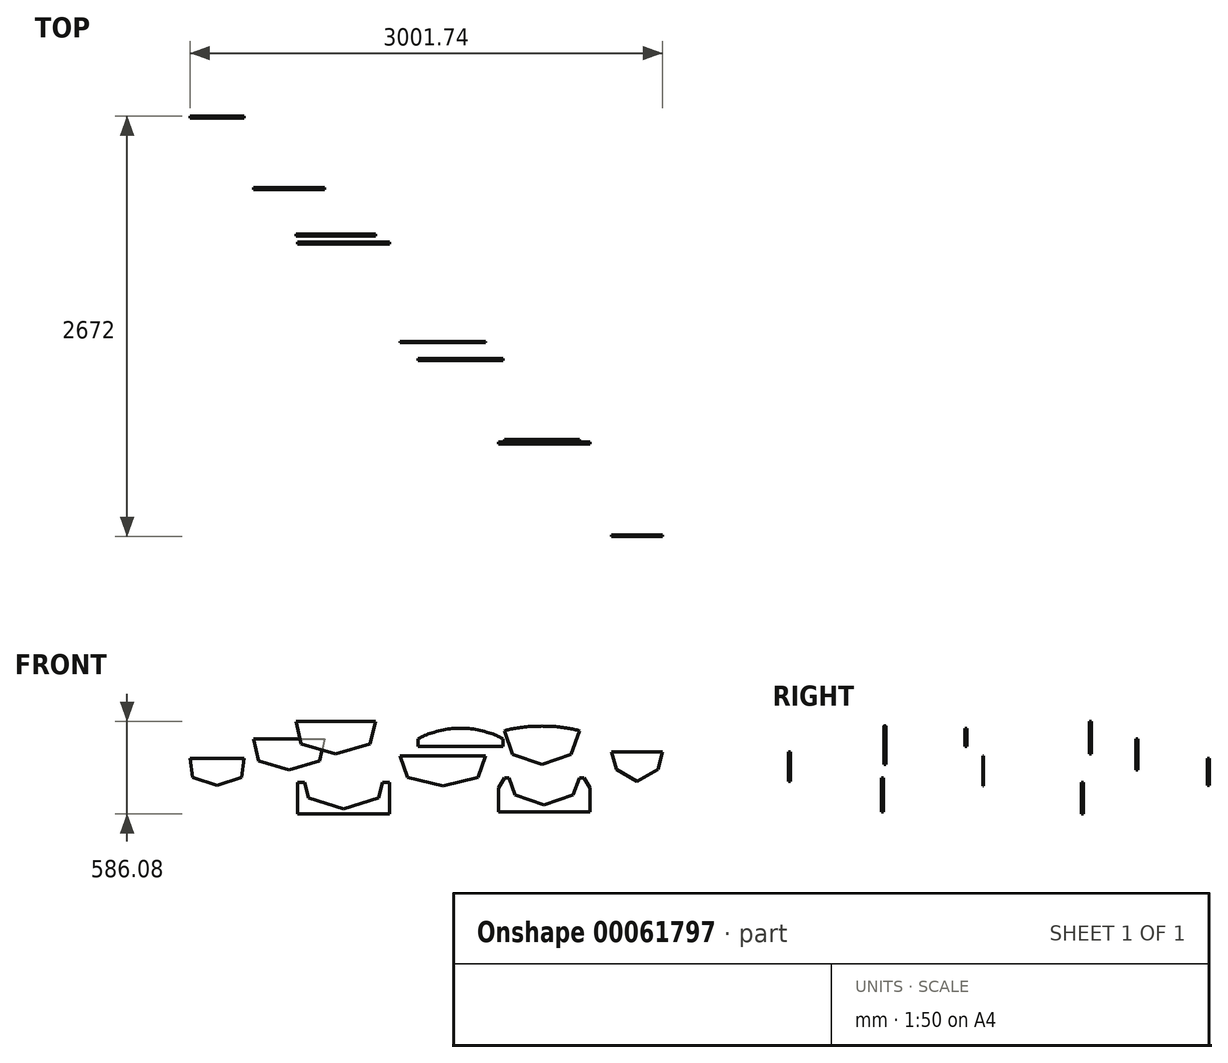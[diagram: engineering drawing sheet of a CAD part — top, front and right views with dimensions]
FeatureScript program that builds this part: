
annotation { "Feature Type Name" : "Feature", "Feature Type Description" : "" }
export const myFeature = defineFeature(function(context is Context, id is Id, definition is map)
    precondition{}
    {
        {
            var Q0;
            Q0=qCreatedBy(makeId("Front.planeOp"),FACE);
            var sketch = newSketch(context, id + "F0", { "sketchPlane" : qUnion([Q0])});
            skLineSegment(sketch, "E0", {"start": v(-1830.68, 262.65) * mm, "end": v(-1200, 262.65) * mm});
            skLineSegment(sketch, "E1", {"start": v(-1830.68, -139.62) * mm, "end": v(-1830.68, 4799.2) * mm, "construction": true});
            skLineSegment(sketch, "E2", {"start": v(-1881.52, 887.8) * mm, "end": v(-1881.52, 681.7) * mm, "construction": true});
            skLineSegment(sketch, "E3", {"start": v(-1881.52, 887.8) * mm, "end": v(-1629.48, 887.8) * mm});
            skLineSegment(sketch, "E4", {"start": v(-1629.48, 887.8) * mm, "end": v(-1663.3, 746.84) * mm});
            skLineSegment(sketch, "E5", {"start": v(-1663.3, 746.84) * mm, "end": v(-1881.52, 681.7) * mm});
            skLineSegment(sketch, "E6", {"start": v(-2176.59, 779.12) * mm, "end": v(-2176.59, 581.77) * mm, "construction": true});
            skLineSegment(sketch, "E7", {"start": v(-2176.59, 779.12) * mm, "end": v(-1951.82, 779.12) * mm});
            skLineSegment(sketch, "E8", {"start": v(-1951.82, 779.12) * mm, "end": v(-1983.36, 639.45) * mm});
            skLineSegment(sketch, "E9", {"start": v(-1983.36, 639.45) * mm, "end": v(-2176.59, 581.77) * mm});
            skLineSegment(sketch, "E10", {"start": v(-2634.04, 652.9) * mm, "end": v(-2634.04, 481.38) * mm, "construction": true});
            skLineSegment(sketch, "E11", {"start": v(-2634.04, 481.38) * mm, "end": v(-2477.4, 532.43) * mm});
            skLineSegment(sketch, "E12", {"start": v(-2477.4, 532.43) * mm, "end": v(-2462.07, 652.9) * mm});
            skLineSegment(sketch, "E13", {"start": v(-2462.07, 652.9) * mm, "end": v(-2634.04, 652.9) * mm});
            skLineSegment(sketch, "E14", {"start": v(-1830.68, 301.72) * mm, "end": v(-1830.68, 334.1) * mm, "construction": true});
            skLineSegment(sketch, "E15", {"start": v(-1830.68, 301.72) * mm, "end": v(-1538.96, 301.72) * mm});
            skLineSegment(sketch, "E16", {"start": v(-1538.96, 301.72) * mm, "end": v(-1538.96, 502.42) * mm});
            skLineSegment(sketch, "E17", {"start": v(-1538.96, 502.42) * mm, "end": v(-1583.2, 502.42) * mm});
            skLineSegment(sketch, "E18", {"start": v(-1583.2, 502.42) * mm, "end": v(-1609.22, 402.47) * mm});
            skLineSegment(sketch, "E19", {"start": v(-1609.22, 402.47) * mm, "end": v(-1830.68, 334.1) * mm});
            skLineSegment(sketch, "E20", {"start": v(-1200.8, 670.27) * mm, "end": v(-1200.8, 478.47) * mm, "construction": true});
            skLineSegment(sketch, "E21", {"start": v(-1200.8, 670.27) * mm, "end": v(-928.1, 670.27) * mm});
            skLineSegment(sketch, "E22", {"start": v(-928.1, 670.27) * mm, "end": v(-976.27, 533.92) * mm});
            skLineSegment(sketch, "E23", {"start": v(-976.27, 533.92) * mm, "end": v(-1200.8, 478.47) * mm});
            skLineSegment(sketch, "E24", {"start": v(-1088.15, 729.97) * mm, "end": v(-818.18, 729.97) * mm});
            skLineSegment(sketch, "E25", {"start": v(-818.18, 729.97) * mm, "end": v(-818.18, 778.33) * mm});
            skLineSegment(sketch, "E26", {"start": v(-1088.15, 729.97) * mm, "end": v(-1088.15, 845.89) * mm, "construction": true});
            skFitSpline(sketch, "E27", {"points": [v(-1088.15, 845.89) * mm, v(-1019.68, 840.48) * mm, v(-959.8, 829.65) * mm, v(-902.8, 814.5) * mm, v(-861.68, 799.35) * mm, v(-818.18, 778.33) * mm], "startDerivative": vector(314.76, -18.35) * mm, "endDerivative": vector(237.16, -119.9) * mm});
            skLineSegment(sketch, "E28", {"start": v(-571.9, 616.82) * mm, "end": v(-571.9, 859.2) * mm, "construction": true});
            skLineSegment(sketch, "E29", {"start": v(-571.9, 616.82) * mm, "end": v(-387.13, 679.24) * mm});
            skLineSegment(sketch, "E30", {"start": v(-387.13, 679.24) * mm, "end": v(-333.5, 829.26) * mm});
            skFitSpline(sketch, "E31", {"points": [v(-571.9, 859.2) * mm, v(-495.31, 856.38) * mm, v(-450.64, 851.56) * mm, v(-419.47, 847.38) * mm, v(-389.9, 842.56) * mm, v(-368.37, 838.39) * mm, v(-346.52, 833.57) * mm, v(-333.5, 829.26) * mm], "startDerivative": vector(367.92, -7.93) * mm, "endDerivative": vector(128.38, -47.16) * mm});
            skLineSegment(sketch, "E32", {"start": v(-557.3, 313.35) * mm, "end": v(-557.3, 357.58) * mm, "construction": true});
            skLineSegment(sketch, "E33", {"start": v(-557.3, 357.58) * mm, "end": v(-373.4, 422.9) * mm});
            skLineSegment(sketch, "E34", {"start": v(-373.4, 422.9) * mm, "end": v(-333.26, 530.39) * mm});
            skLineSegment(sketch, "E35", {"start": v(-333.26, 530.39) * mm, "end": v(-305.1, 530.39) * mm});
            skLineSegment(sketch, "E36", {"start": v(-305.1, 530.39) * mm, "end": v(-266.92, 466.71) * mm});
            skLineSegment(sketch, "E37", {"start": v(-266.92, 466.71) * mm, "end": v(-266.92, 313.35) * mm});
            skLineSegment(sketch, "E38", {"start": v(-557.3, 313.35) * mm, "end": v(-266.92, 313.35) * mm});
            skPoint(sketch, "E39.orphan", {"position": v(-266.92, 314.51) * mm});
            skLineSegment(sketch, "E40", {"start": v(33.12, 696.1) * mm, "end": v(33.12, 509.05) * mm, "construction": true});
            skLineSegment(sketch, "E41", {"start": v(33.12, 696.1) * mm, "end": v(195.74, 696.1) * mm});
            skLineSegment(sketch, "E42", {"start": v(195.74, 696.1) * mm, "end": v(164.42, 585.63) * mm});
            skLineSegment(sketch, "E43", {"start": v(164.42, 585.63) * mm, "end": v(33.12, 509.05) * mm});
            skSolve(sketch);
        }
        {
            var Q0;
            Q0=qCreatedBy(makeId("Front.planeOp"),FACE);
            cPlane(context, id + "F1", {"entities" : qUnion([Q0]), "cplaneType" : CPlaneType.OFFSET, "offset" : 50 * mm, "oppositeDirection" : true, "width" : 150 * mm, "height" : 150 * mm});
        }
        {
            var Q0;
            Q0=qCreatedBy(id+"F1.planeOp",FACE);
            var sketch = newSketch(context, id + "F2", { "sketchPlane" : qUnion([Q0])});
            skLineSegment(sketch, "E44.0", {"start": v(-1663.3, 746.84) * mm, "end": v(-1881.52, 681.7) * mm});
            skLineSegment(sketch, "E45.0", {"start": v(-1629.48, 887.8) * mm, "end": v(-1663.3, 746.84) * mm});
            skLineSegment(sketch, "E46.0", {"start": v(-1881.52, 887.8) * mm, "end": v(-1629.48, 887.8) * mm});
            skLineSegment(sketch, "E47.0", {"start": v(-1881.52, 887.8) * mm, "end": v(-1881.52, 681.7) * mm});
            skLineSegment(sketch, "E48.MirrorCS", {"start": v(-1881.52, 887.8) * mm, "end": v(-2133.56, 887.8) * mm});
            skLineSegment(sketch, "E49.MirrorCS", {"start": v(-2133.56, 887.8) * mm, "end": v(-2099.74, 746.84) * mm});
            skLineSegment(sketch, "E50.MirrorCS", {"start": v(-2099.74, 746.84) * mm, "end": v(-1881.52, 681.7) * mm});
            skSolve(sketch);
        }
        {
            var Q0;
            Q0 = qSketchRegion(id + "F2", true);
            extrude(context, id + "F3", {"entities" : qUnion([Q0]), "endBound" : BoundingType.SYMMETRIC, "depth" : 12 * mm});
        }
        {
            var Q0;
            Q0=qCreatedBy(makeId("Front.planeOp"),FACE);
            cPlane(context, id + "F4", {"entities" : qUnion([Q0]), "cplaneType" : CPlaneType.OFFSET, "offset" : 345 * mm, "oppositeDirection" : true, "width" : 150 * mm, "height" : 150 * mm});
        }
        {
            var Q0;
            Q0=qCreatedBy(id+"F4.planeOp",FACE);
            var sketch = newSketch(context, id + "F5", { "sketchPlane" : qUnion([Q0])});
            skLineSegment(sketch, "E51.0", {"start": v(-1983.36, 639.45) * mm, "end": v(-2176.59, 581.77) * mm});
            skLineSegment(sketch, "E51.1", {"start": v(-1951.82, 779.12) * mm, "end": v(-1983.36, 639.45) * mm});
            skLineSegment(sketch, "E51.2", {"start": v(-2176.59, 779.12) * mm, "end": v(-1951.82, 779.12) * mm});
            skLineSegment(sketch, "E51.3", {"start": v(-2176.59, 779.12) * mm, "end": v(-2176.59, 581.77) * mm});
            skLineSegment(sketch, "E52.MirrorCS", {"start": v(-2176.59, 779.12) * mm, "end": v(-2401.35, 779.12) * mm});
            skLineSegment(sketch, "E53.MirrorCS", {"start": v(-2401.35, 779.12) * mm, "end": v(-2369.8, 639.45) * mm});
            skLineSegment(sketch, "E54.MirrorCS", {"start": v(-2369.8, 639.45) * mm, "end": v(-2176.59, 581.77) * mm});
            skSolve(sketch);
        }
        {
            var Q0;
            Q0 = qSketchRegion(id + "F5", true);
            extrude(context, id + "F6", {"entities" : qUnion([Q0]), "endBound" : BoundingType.SYMMETRIC, "depth" : 12 * mm});
        }
        {
            var Q0;
            Q0=qCreatedBy(makeId("Front.planeOp"),FACE);
            var sketch = newSketch(context, id + "F7", { "sketchPlane" : qUnion([Q0])});
            skLineSegment(sketch, "E55.0", {"start": v(-1609.22, 402.47) * mm, "end": v(-1830.68, 334.1) * mm});
            skLineSegment(sketch, "E56.0", {"start": v(-1583.2, 502.42) * mm, "end": v(-1609.22, 402.47) * mm});
            skLineSegment(sketch, "E57.0", {"start": v(-1538.96, 502.42) * mm, "end": v(-1583.2, 502.42) * mm});
            skLineSegment(sketch, "E58.0", {"start": v(-1538.96, 301.72) * mm, "end": v(-1538.96, 502.42) * mm});
            skLineSegment(sketch, "E59.0", {"start": v(-1830.68, 301.72) * mm, "end": v(-1538.96, 301.72) * mm});
            skLineSegment(sketch, "E60.0", {"start": v(-1830.68, 301.72) * mm, "end": v(-1830.68, 334.1) * mm, "construction": true});
            skLineSegment(sketch, "E61", {"start": v(-1830.68, 334.1) * mm, "end": v(-1830.68, 301.72) * mm, "construction": true});
            skLineSegment(sketch, "E62.MirrorCS", {"start": v(-2052.14, 402.47) * mm, "end": v(-1830.68, 334.1) * mm});
            skLineSegment(sketch, "E63.MirrorCS", {"start": v(-2078.17, 502.42) * mm, "end": v(-2052.14, 402.47) * mm});
            skLineSegment(sketch, "E64.MirrorCS", {"start": v(-2122.4, 502.42) * mm, "end": v(-2078.17, 502.42) * mm});
            skLineSegment(sketch, "E65.MirrorCS", {"start": v(-2122.4, 301.72) * mm, "end": v(-2122.4, 502.42) * mm});
            skLineSegment(sketch, "E66.MirrorCS", {"start": v(-1830.68, 301.72) * mm, "end": v(-2122.4, 301.72) * mm});
            skSolve(sketch);
        }
        {
            var Q0;
            Q0 = qSketchRegion(id + "F7", true);
            extrude(context, id + "F8", {"entities" : qUnion([Q0]), "endBound" : BoundingType.SYMMETRIC, "depth" : 12 * mm});
        }
        {
            var Q0;
            Q0=qCreatedBy(makeId("Front.planeOp"),FACE);
            cPlane(context, id + "F9", {"entities" : qUnion([Q0]), "cplaneType" : CPlaneType.OFFSET, "offset" : 800 * mm, "oppositeDirection" : true, "width" : 150 * mm, "height" : 150 * mm});
        }
        {
            var Q0;
            Q0=qCreatedBy(id+"F9.planeOp",FACE);
            var sketch = newSketch(context, id + "F10", { "sketchPlane" : qUnion([Q0])});
            skLineSegment(sketch, "E67.0", {"start": v(-2462.07, 652.9) * mm, "end": v(-2634.04, 652.9) * mm});
            skLineSegment(sketch, "E68.0", {"start": v(-2477.4, 532.43) * mm, "end": v(-2462.07, 652.9) * mm});
            skLineSegment(sketch, "E69.0", {"start": v(-2634.04, 481.38) * mm, "end": v(-2477.4, 532.43) * mm});
            skLineSegment(sketch, "E70.0", {"start": v(-2634.04, 652.9) * mm, "end": v(-2634.04, 481.38) * mm});
            skLineSegment(sketch, "E71.MirrorCS", {"start": v(-2806, 652.9) * mm, "end": v(-2634.04, 652.9) * mm});
            skLineSegment(sketch, "E72.MirrorCS", {"start": v(-2790.68, 532.43) * mm, "end": v(-2806, 652.9) * mm});
            skLineSegment(sketch, "E73.MirrorCS", {"start": v(-2634.04, 481.38) * mm, "end": v(-2790.68, 532.43) * mm});
            skSolve(sketch);
        }
        {
            var Q0;
            Q0 = qSketchRegion(id + "F10", true);
            extrude(context, id + "F11", {"entities" : qUnion([Q0]), "endBound" : BoundingType.SYMMETRIC, "depth" : 12 * mm});
        }
        {
            var Q0;
            Q0=qCreatedBy(makeId("Front.planeOp"),FACE);
            cPlane(context, id + "F12", {"entities" : qUnion([Q0]), "cplaneType" : CPlaneType.OFFSET, "offset" : 630 * mm, "width" : 150 * mm, "height" : 150 * mm});
        }
        {
            var Q0;
            Q0=qCreatedBy(id+"F12.planeOp",FACE);
            var sketch = newSketch(context, id + "F13", { "sketchPlane" : qUnion([Q0])});
            skLineSegment(sketch, "E74.0", {"start": v(-1200.8, 670.27) * mm, "end": v(-928.1, 670.27) * mm});
            skLineSegment(sketch, "E75.1", {"start": v(-928.1, 670.27) * mm, "end": v(-976.27, 533.92) * mm});
            skLineSegment(sketch, "E76.0", {"start": v(-976.27, 533.92) * mm, "end": v(-1200.8, 478.47) * mm});
            skLineSegment(sketch, "E77.0", {"start": v(-1200.8, 670.27) * mm, "end": v(-1200.8, 478.47) * mm, "construction": true});
            skLineSegment(sketch, "E78.MirrorCS", {"start": v(-1425.32, 533.92) * mm, "end": v(-1200.8, 478.47) * mm});
            skLineSegment(sketch, "E79.MirrorCS", {"start": v(-1473.5, 670.27) * mm, "end": v(-1425.32, 533.92) * mm});
            skLineSegment(sketch, "E80.MirrorCS", {"start": v(-1200.8, 670.27) * mm, "end": v(-1473.5, 670.27) * mm});
            skSolve(sketch);
        }
        {
            var Q0;
            Q0=makeQuery(id+"F13.imprint","IMPRINT",FACE,{"disambiguationData":[TD([[makeQuery(id+"F13.imprint","IMPRINT",EDGE,{"derivedFrom":sQuery(id+"F13.wireOp",EDGE,"E74.0")}),-1.0]])]});
            extrude(context, id + "F14", {"entities" : qUnion([Q0]), "endBound" : BoundingType.SYMMETRIC, "depth" : 4 * mm});
        }
        {
            var Q0;
            Q0=qCreatedBy(makeId("Front.planeOp"),FACE);
            cPlane(context, id + "F15", {"entities" : qUnion([Q0]), "cplaneType" : CPlaneType.OFFSET, "offset" : 740 * mm, "width" : 150 * mm, "height" : 150 * mm});
        }
        {
            var Q0;
            Q0=qCreatedBy(id+"F15.planeOp",FACE);
            var sketch = newSketch(context, id + "F16", { "sketchPlane" : qUnion([Q0])});
            skFitSpline(sketch, "E81.0", {"points": [v(-1088.15, 845.89) * mm, v(-1064.86, 844.53) * mm, v(-1019.66, 841.9) * mm, v(-960.64, 830.55) * mm, v(-902.76, 815.3) * mm, v(-861.63, 800.3) * mm, v(-832.9, 785.77) * mm, v(-818.18, 778.33) * mm]});
            skLineSegment(sketch, "E82.0", {"start": v(-818.18, 729.97) * mm, "end": v(-818.18, 778.33) * mm});
            skLineSegment(sketch, "E83.0", {"start": v(-1088.15, 729.97) * mm, "end": v(-818.18, 729.97) * mm});
            skLineSegment(sketch, "E84.0", {"start": v(-1088.15, 729.97) * mm, "end": v(-1088.15, 845.89) * mm});
            skFitSpline(sketch, "E85.MirrorCS", {"points": [v(-1088.15, 845.89) * mm, v(-1111.44, 844.53) * mm, v(-1156.64, 841.9) * mm, v(-1215.67, 830.55) * mm, v(-1273.54, 815.3) * mm, v(-1314.67, 800.3) * mm, v(-1343.4, 785.77) * mm, v(-1358.12, 778.33) * mm]});
            skLineSegment(sketch, "E86.MirrorCS", {"start": v(-1358.12, 729.97) * mm, "end": v(-1358.12, 778.33) * mm});
            skLineSegment(sketch, "E87.MirrorCS", {"start": v(-1088.15, 729.97) * mm, "end": v(-1358.12, 729.97) * mm});
            skSolve(sketch);
        }
        {
            var Q0;
            Q0 = qSketchRegion(id + "F16", true);
            extrude(context, id + "F17", {"entities" : qUnion([Q0]), "endBound" : BoundingType.SYMMETRIC, "depth" : 12 * mm});
        }
        {
            var Q0;
            Q0=qCreatedBy(makeId("Front.planeOp"),FACE);
            cPlane(context, id + "F18", {"entities" : qUnion([Q0]), "cplaneType" : CPlaneType.OFFSET, "offset" : 1255 * mm, "width" : 150 * mm, "height" : 150 * mm});
        }
        {
            var Q0;
            Q0=qCreatedBy(id+"F18.planeOp",FACE);
            var sketch = newSketch(context, id + "F19", { "sketchPlane" : qUnion([Q0])});
            skLineSegment(sketch, "E88.0", {"start": v(-571.9, 616.82) * mm, "end": v(-387.13, 679.24) * mm});
            skLineSegment(sketch, "E89.0", {"start": v(-387.13, 679.24) * mm, "end": v(-333.5, 829.26) * mm});
            skFitSpline(sketch, "E90.0", {"points": [v(-571.9, 859.2) * mm, v(-544.82, 858.61) * mm, v(-497.01, 857.58) * mm, v(-451.59, 851.67) * mm, v(-420.13, 847.67) * mm, v(-389.9, 842.72) * mm, v(-369.02, 838.5) * mm, v(-346.6, 834.07) * mm, v(-337.5, 830.73) * mm, v(-333.5, 829.26) * mm]});
            skLineSegment(sketch, "E91.0", {"start": v(-571.9, 616.82) * mm, "end": v(-571.9, 859.2) * mm, "construction": true});
            skFitSpline(sketch, "E92.MirrorCS", {"points": [v(-571.9, 859.2) * mm, v(-598.97, 858.61) * mm, v(-646.77, 857.58) * mm, v(-692.2, 851.67) * mm, v(-723.66, 847.67) * mm, v(-753.89, 842.72) * mm, v(-774.77, 838.5) * mm, v(-797.18, 834.07) * mm, v(-806.28, 830.73) * mm, v(-810.28, 829.26) * mm]});
            skLineSegment(sketch, "E93.MirrorCS", {"start": v(-756.65, 679.24) * mm, "end": v(-810.28, 829.26) * mm});
            skLineSegment(sketch, "E94.MirrorCS", {"start": v(-571.9, 616.82) * mm, "end": v(-756.65, 679.24) * mm});
            skSolve(sketch);
        }
        {
            var Q0;
            Q0=makeQuery(id+"F19.imprint","IMPRINT",FACE,{"disambiguationData":[TD([[makeQuery(id+"F19.imprint","IMPRINT",EDGE,{"derivedFrom":sQuery(id+"F19.wireOp",EDGE,"E88.0")}),1.0]])]});
            extrude(context, id + "F20", {"entities" : qUnion([Q0]), "endBound" : BoundingType.SYMMETRIC, "depth" : 12 * mm});
        }
        {
            var Q0;
            Q0=qCreatedBy(makeId("Front.planeOp"),FACE);
            cPlane(context, id + "F21", {"entities" : qUnion([Q0]), "cplaneType" : CPlaneType.OFFSET, "offset" : 1270 * mm, "width" : 150 * mm, "height" : 150 * mm});
        }
        {
            var Q0;
            Q0=qCreatedBy(id+"F21.planeOp",FACE);
            var sketch = newSketch(context, id + "F22", { "sketchPlane" : qUnion([Q0])});
            skLineSegment(sketch, "E95.0", {"start": v(-557.3, 313.35) * mm, "end": v(-266.92, 313.35) * mm});
            skLineSegment(sketch, "E96.0", {"start": v(-266.92, 466.71) * mm, "end": v(-266.92, 313.35) * mm});
            skLineSegment(sketch, "E97.0", {"start": v(-305.1, 530.39) * mm, "end": v(-266.92, 466.71) * mm});
            skLineSegment(sketch, "E98.0", {"start": v(-333.26, 530.39) * mm, "end": v(-305.1, 530.39) * mm});
            skLineSegment(sketch, "E99.0", {"start": v(-373.4, 422.9) * mm, "end": v(-333.26, 530.39) * mm});
            skLineSegment(sketch, "E100.0", {"start": v(-557.3, 357.58) * mm, "end": v(-373.4, 422.9) * mm});
            skLineSegment(sketch, "E101.0", {"start": v(-557.3, 313.35) * mm, "end": v(-557.3, 357.58) * mm, "construction": true});
            skLineSegment(sketch, "E102.MirrorCS", {"start": v(-557.3, 357.58) * mm, "end": v(-741.21, 422.9) * mm});
            skLineSegment(sketch, "E103.MirrorCS", {"start": v(-741.21, 422.9) * mm, "end": v(-781.36, 530.39) * mm});
            skLineSegment(sketch, "E104.MirrorCS", {"start": v(-781.36, 530.39) * mm, "end": v(-809.52, 530.39) * mm});
            skLineSegment(sketch, "E105.MirrorCS", {"start": v(-809.52, 530.39) * mm, "end": v(-847.7, 466.71) * mm});
            skLineSegment(sketch, "E106.MirrorCS", {"start": v(-847.7, 466.71) * mm, "end": v(-847.7, 313.35) * mm});
            skLineSegment(sketch, "E107.MirrorCS", {"start": v(-557.3, 313.35) * mm, "end": v(-847.7, 313.35) * mm});
            skSolve(sketch);
        }
        {
            var Q0;
            Q0 = qSketchRegion(id + "F22", true);
            extrude(context, id + "F23", {"entities" : qUnion([Q0]), "endBound" : BoundingType.SYMMETRIC, "depth" : 12 * mm});
        }
        {
            var Q0;
            Q0=qCreatedBy(makeId("Front.planeOp"),FACE);
            cPlane(context, id + "F24", {"entities" : qUnion([Q0]), "cplaneType" : CPlaneType.OFFSET, "offset" : 1860 * mm, "width" : 150 * mm, "height" : 150 * mm});
        }
        {
            var Q0;
            Q0=qCreatedBy(id+"F24.planeOp",FACE);
            var sketch = newSketch(context, id + "F25", { "sketchPlane" : qUnion([Q0])});
            skLineSegment(sketch, "E108.0", {"start": v(164.42, 585.63) * mm, "end": v(33.12, 509.05) * mm});
            skLineSegment(sketch, "E109.0", {"start": v(195.74, 696.1) * mm, "end": v(164.42, 585.63) * mm});
            skLineSegment(sketch, "E110.0", {"start": v(33.12, 696.1) * mm, "end": v(195.74, 696.1) * mm});
            skLineSegment(sketch, "E111.0", {"start": v(33.12, 696.1) * mm, "end": v(33.12, 509.05) * mm, "construction": true});
            skLineSegment(sketch, "E112.MirrorCS", {"start": v(33.12, 696.1) * mm, "end": v(-129.5, 696.1) * mm});
            skLineSegment(sketch, "E113.MirrorCS", {"start": v(-129.5, 696.1) * mm, "end": v(-98.18, 585.63) * mm});
            skLineSegment(sketch, "E114.MirrorCS", {"start": v(-98.18, 585.63) * mm, "end": v(33.12, 509.05) * mm});
            skSolve(sketch);
        }
        {
            var Q0;
            Q0 = qSketchRegion(id + "F25", true);
            extrude(context, id + "F26", {"entities" : qUnion([Q0]), "endBound" : BoundingType.SYMMETRIC, "depth" : 12 * mm});
        }
    });
